# Revit family: 3D-AKE-00020629
name_source: partatom
category: Sonderausstattung
units: mm (PartAtom-declared; Revit-internal decimal feet)

## family parameters
Arbeitsebenenbasiert = Nein
Beim Laden mit Abzugskörper schneiden = Nein
Bemaßung runder Anschluss = Durchmesser verwenden
Beschriftungsausrichtung beibehalten = Nein
Gemeinsam genutzt = Nein
Immer vertikal = Ja
OmniClass-Nummer = 23.40.40.11.21
OmniClass-Titel = Hot Cabinets
Raumberechnungspunkt = Nein
Schneiden in Ansichten zulassen = Ja
Teiletyp = Normal

## types (1)
- Norm
    Abwicklungshöhe = 0
    Abwicklungslänge = 0
    Artikelvorlage = 00900016
    Bauteilnummer = 3D-AKE-00020629
    Beschreibung = Umluftwärmevitrine
    Breite = 596
    DocNumber = 3D-AKE-00020591.ipt
    Entstanden aus = 3D-AKE-00020591.ipt
    Ersatzteilkennung = nein
    Erstellungsdatum = 12.02.2019
    Folder = Produkte\Standardzeichnungen\
    Genehmigungsdatum Konstr. = 10.03.2023
    Gewicht = 48,8 kg
    Hersteller = AKE
    Höhe = 770
    Kennung = Standardteil
    Konstruktionsstatus = 1
    Modell = Hot Vario 1
    Tiefe = 786,4
    Titel = Hot Vario 2
    URL = www.ideal-ake.at
    VDS_Category = 3D-Konstruktion Kundendaten
    Vorgabe-Ansicht = 0 mm  [stored 0 ft]

note: [stored X ft] marks values corroborated as IEEE doubles in the binary element streams (Revit-internal decimal feet)
